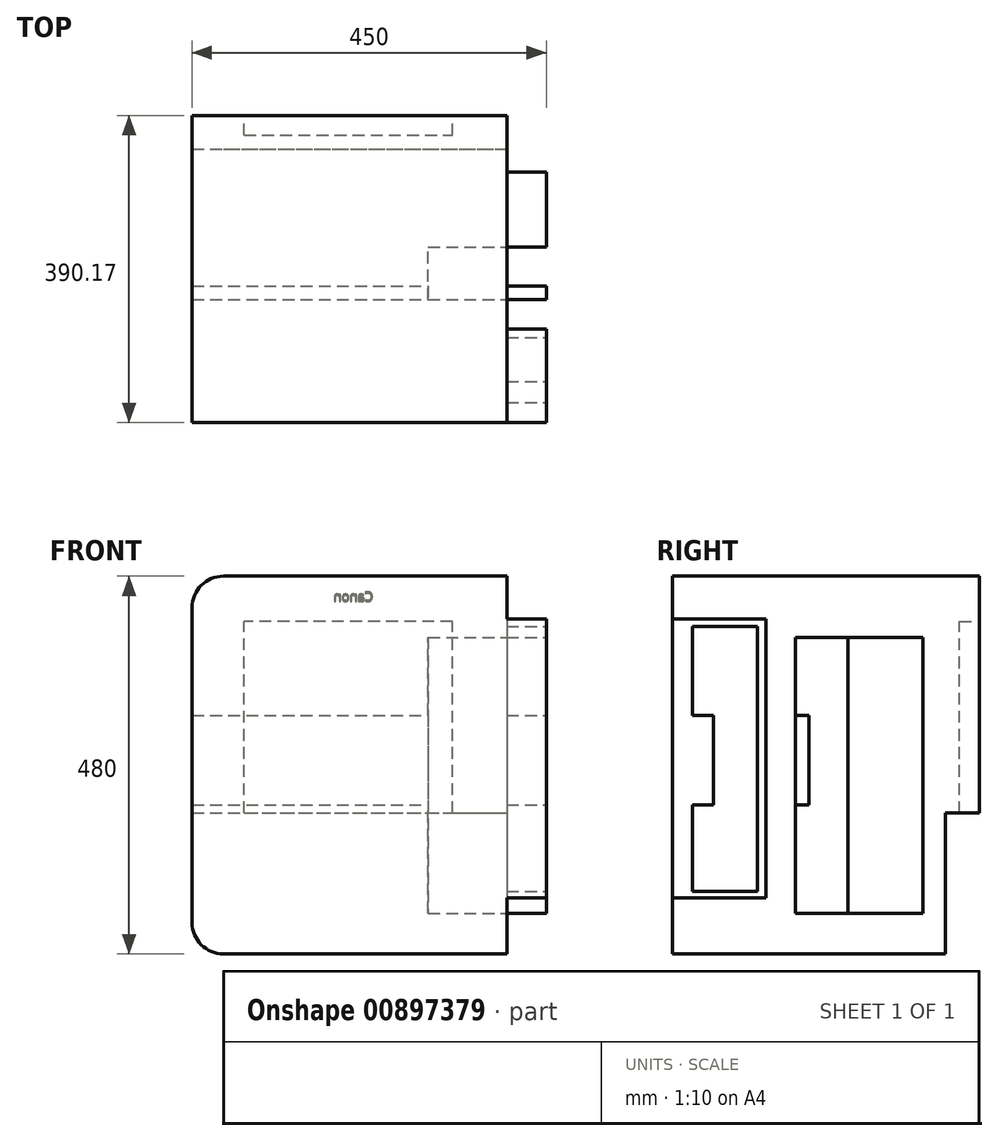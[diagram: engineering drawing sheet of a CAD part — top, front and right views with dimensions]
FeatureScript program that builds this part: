
annotation { "Feature Type Name" : "Feature", "Feature Type Description" : "" }
export const myFeature = defineFeature(function(context is Context, id is Id, definition is map)
    precondition{}
    {
        {
            var Q0;
            Q0=qCreatedBy(makeId("Top.planeOp"),FACE);
            var sketch = newSketch(context, id + "F0", { "sketchPlane" : qUnion([Q0])});
            skLineSegment(sketch, "E0.bottom", {"start": v(0, 0) * mm, "end": v(-450, 0) * mm});
            skLineSegment(sketch, "E0.top", {"start": v(0, 390) * mm, "end": v(-450, 390) * mm});
            skLineSegment(sketch, "E0.left", {"start": v(0, 0) * mm, "end": v(0, 390) * mm});
            skLineSegment(sketch, "E0.right", {"start": v(-450, 0) * mm, "end": v(-450, 390) * mm});
            skSolve(sketch);
        }
        {
            var Q0;
            Q0 = qSketchRegion(id + "F0", true);
            extrude(context, id + "F1", {"entities" : qUnion([Q0]), "depth" : 480 * mm, "offsetDistance" : 25 * mm});
        }
        {
            var Q0;
            Q0=makeQuery(id+"F1.opExtrude","SWEPT_FACE",FACE,{"disambiguationData":[OSD([sQuery(id+"F0.wireOp",EDGE,"E0.left")])]});
            var sketch = newSketch(context, id + "F2", { "sketchPlane" : qUnion([Q0])});
            skLineSegment(sketch, "E1.bottom", {"start": v(390, 480) * mm, "end": v(318.17, 480) * mm});
            skLineSegment(sketch, "E1.top", {"start": v(390, 0) * mm, "end": v(318.17, 0) * mm});
            skLineSegment(sketch, "E1.left", {"start": v(390, 480) * mm, "end": v(390, 0) * mm});
            skLineSegment(sketch, "E1.right", {"start": v(318.17, 480) * mm, "end": v(318.17, 0) * mm});
            skLineSegment(sketch, "E2.bottom", {"start": v(223.33, 480) * mm, "end": v(173.64, 480) * mm});
            skLineSegment(sketch, "E2.top", {"start": v(223.33, 0) * mm, "end": v(173.64, 0) * mm});
            skLineSegment(sketch, "E2.left", {"start": v(223.33, 480) * mm, "end": v(223.33, 0) * mm});
            skLineSegment(sketch, "E2.right", {"start": v(173.64, 480) * mm, "end": v(173.64, 0) * mm});
            skLineSegment(sketch, "E3.bottom", {"start": v(318.17, 480) * mm, "end": v(223.33, 480) * mm});
            skLineSegment(sketch, "E3.top", {"start": v(318.17, 402.26) * mm, "end": v(223.33, 402.26) * mm});
            skLineSegment(sketch, "E3.left", {"start": v(318.17, 480) * mm, "end": v(318.17, 402.26) * mm});
            skLineSegment(sketch, "E3.right", {"start": v(223.33, 480) * mm, "end": v(223.33, 402.26) * mm});
            skLineSegment(sketch, "E4.bottom", {"start": v(318.17, 0) * mm, "end": v(223.33, 0) * mm});
            skLineSegment(sketch, "E4.top", {"start": v(318.17, 51.83) * mm, "end": v(223.33, 51.83) * mm});
            skLineSegment(sketch, "E4.left", {"start": v(318.17, 0) * mm, "end": v(318.17, 51.83) * mm});
            skLineSegment(sketch, "E4.right", {"start": v(223.33, 0) * mm, "end": v(223.33, 51.83) * mm});
            skLineSegment(sketch, "E5.bottom", {"start": v(173.64, 303.3) * mm, "end": v(156.24, 303.3) * mm});
            skLineSegment(sketch, "E5.top", {"start": v(173.64, 189.66) * mm, "end": v(156.24, 189.66) * mm});
            skLineSegment(sketch, "E5.left", {"start": v(173.64, 303.3) * mm, "end": v(173.64, 189.66) * mm});
            skLineSegment(sketch, "E5.right", {"start": v(156.24, 303.3) * mm, "end": v(156.24, 189.66) * mm});
            skLineSegment(sketch, "E6.bottom", {"start": v(0, 425.5) * mm, "end": v(25.82, 425.5) * mm});
            skLineSegment(sketch, "E6.top", {"start": v(0, 71.14) * mm, "end": v(25.82, 71.14) * mm});
            skLineSegment(sketch, "E6.left", {"start": v(0, 425.5) * mm, "end": v(0, 71.14) * mm});
            skLineSegment(sketch, "E6.right", {"start": v(25.82, 425.5) * mm, "end": v(25.82, 71.14) * mm});
            skLineSegment(sketch, "E7.bottom", {"start": v(25.82, 425.5) * mm, "end": v(119.02, 425.5) * mm});
            skLineSegment(sketch, "E7.top", {"start": v(25.82, 71.14) * mm, "end": v(119.02, 71.14) * mm});
            skLineSegment(sketch, "E7.right", {"start": v(119.02, 425.5) * mm, "end": v(119.02, 71.14) * mm});
            skLineSegment(sketch, "E8.bottom", {"start": v(25.82, 416.3) * mm, "end": v(108.06, 416.3) * mm});
            skLineSegment(sketch, "E8.top", {"start": v(25.82, 79.57) * mm, "end": v(108.06, 79.57) * mm});
            skLineSegment(sketch, "E8.left", {"start": v(25.82, 416.3) * mm, "end": v(25.82, 79.57) * mm});
            skLineSegment(sketch, "E8.right", {"start": v(108.06, 416.3) * mm, "end": v(108.06, 79.57) * mm});
            skLineSegment(sketch, "E9.bottom", {"start": v(25.82, 303.3) * mm, "end": v(52.47, 303.3) * mm});
            skLineSegment(sketch, "E9.top", {"start": v(25.82, 189.66) * mm, "end": v(52.47, 189.66) * mm});
            skLineSegment(sketch, "E9.left", {"start": v(25.82, 303.3) * mm, "end": v(25.82, 189.66) * mm});
            skLineSegment(sketch, "E9.right", {"start": v(52.47, 303.3) * mm, "end": v(52.47, 189.66) * mm});
            skSolve(sketch);
        }
        {
            var Q0;
            {var subQ1=sQuery(id+"F2.wireOp",EDGE,"E2.bottom");Q0=makeQuery(id+"F2.imprint","IMPRINT",FACE,{"disambiguationData":[TD([[makeQuery(id+"F2.imprint","IMPRINT",EDGE,{"derivedFrom":subQ1}),-1.0]])]});}
            var Q1;
            {var subQ2=sQuery(id+"F2.wireOp",EDGE,"E5.bottom");Q1=makeQuery(id+"F2.imprint","IMPRINT",FACE,{"disambiguationData":[TD([[makeQuery(id+"F2.imprint","IMPRINT",EDGE,{"derivedFrom":subQ2}),-1.0]])]});}
            var Q2;
            {var subQ5=sQuery(id+"F2.wireOp",EDGE,"E8.bottom");Q2=makeQuery(id+"F2.imprint","IMPRINT",FACE,{"disambiguationData":[TD([[makeQuery(id+"F2.imprint","IMPRINT",EDGE,{"derivedFrom":subQ5}),-1.0]])]});}
            var Q3;
            Q3=makeQuery(id+"F2.imprint","IMPRINT",FACE,{"disambiguationData":[TD([[makeQuery(id+"F2.imprint","IMPRINT",EDGE,{"derivedFrom":sQuery(id+"F2.wireOp",EDGE,"E1.bottom")}),-1.0]])]});
            var Q4;
            Q4=makeQuery(id+"F2.imprint","IMPRINT",FACE,{"disambiguationData":[TD([[makeQuery(id+"F2.imprint","IMPRINT",EDGE,{"derivedFrom":sQuery(id+"F2.wireOp",EDGE,"E4.bottom")}),1.0]])]});
            var Q5;
            Q5=makeQuery(id+"F2.imprint","IMPRINT",FACE,{"disambiguationData":[TD([[makeQuery(id+"F2.imprint","IMPRINT",EDGE,{"derivedFrom":sQuery(id+"F2.wireOp",EDGE,"E3.bottom")}),-1.0]])]});
            extrude(context, id + "F3", {"entities" : qUnion([Q0, Q1, Q2, Q3, Q4, Q5]), "operationType" : NewBodyOperationType.REMOVE, "oppositeDirection" : true, "depth" : 50 * mm, "offsetDistance" : 25 * mm});
        }
        {
            var Q0;
            Q0=makeQuery(id+"F3.boolean.opBoolean","COPY",FACE,{"derivedFrom":makeQuery(id+"F3.opExtrude","CAP_FACE",FACE,{"disambiguationData":[OSD([sQuery(id+"F0.wireOp",EDGE,"E0.bottom"),sQuery(id+"F0.wireOp",EDGE,"E0.left"),sQuery(id+"F2.wireOp",EDGE,"E1.bottom"),sQuery(id+"F2.wireOp",EDGE,"E1.top"),sQuery(id+"F2.wireOp",EDGE,"E1.left"),sQuery(id+"F2.wireOp",EDGE,"E1.right"),sQuery(id+"F2.wireOp",EDGE,"E2.bottom"),sQuery(id+"F2.wireOp",EDGE,"E2.top"),sQuery(id+"F2.wireOp",EDGE,"E2.left"),sQuery(id+"F2.wireOp",EDGE,"E3.bottom"),sQuery(id+"F2.wireOp",EDGE,"E3.top"),sQuery(id+"F2.wireOp",EDGE,"E4.bottom"),sQuery(id+"F2.wireOp",EDGE,"E4.top"),sQuery(id+"F2.wireOp",EDGE,"E5.bottom"),sQuery(id+"F2.wireOp",EDGE,"E5.top"),sQuery(id+"F2.wireOp",EDGE,"E5.left"),sQuery(id+"F2.wireOp",EDGE,"E5.right"),sQuery(id+"F2.wireOp",EDGE,"E6.bottom"),sQuery(id+"F2.wireOp",EDGE,"E6.top"),sQuery(id+"F2.wireOp",EDGE,"E7.bottom"),sQuery(id+"F2.wireOp",EDGE,"E7.top"),sQuery(id+"F2.wireOp",EDGE,"E7.right")])],"isStart":false})});
            var sketch = newSketch(context, id + "F4", { "sketchPlane" : qUnion([Q0])});
            skLineSegment(sketch, "E10.bottom", {"start": v(156.24, 51.83) * mm, "end": v(223.33, 51.83) * mm});
            skLineSegment(sketch, "E10.top", {"start": v(156.24, 402.26) * mm, "end": v(223.33, 402.26) * mm});
            skLineSegment(sketch, "E10.left", {"start": v(156.24, 51.83) * mm, "end": v(156.24, 402.26) * mm});
            skLineSegment(sketch, "E10.right", {"start": v(223.33, 51.83) * mm, "end": v(223.33, 402.26) * mm});
            skLineSegment(sketch, "E11.bottom", {"start": v(390, 178.91) * mm, "end": v(347.26, 178.91) * mm});
            skLineSegment(sketch, "E11.top", {"start": v(390, 0) * mm, "end": v(347.26, 0) * mm});
            skLineSegment(sketch, "E11.left", {"start": v(390, 178.91) * mm, "end": v(390, 0) * mm});
            skLineSegment(sketch, "E11.right", {"start": v(347.26, 178.91) * mm, "end": v(347.26, 0) * mm});
            skSolve(sketch);
        }
        {
            var Q0;
            Q0=makeQuery(id+"F4.imprint","IMPRINT",FACE,{"disambiguationData":[TD([[makeQuery(id+"F4.imprint","IMPRINT",EDGE,{"derivedFrom":sQuery(id+"F4.wireOp",EDGE,"E11.bottom")}),1.0]])]});
            var Q1;
            {var subQ1=makeQuery(id+"F3.boolean.opBoolean","COPY",EDGE,{"derivedFrom":makeQuery(id+"F3.opExtrude","CAP_EDGE",EDGE,{"disambiguationData":[OSD([sQuery(id+"F2.wireOp",EDGE,"E5.bottom")])],"isStart":false})});Q1=makeQuery(id+"F4.imprint","IMPRINT",FACE,{"disambiguationData":[TD([[makeQuery(id+"F4.imprint","IMPRINT",EDGE,{"derivedFrom":subQ1}),1.0]])]});}
            extrude(context, id + "F5", {"entities" : qUnion([Q0, Q1]), "operationType" : NewBodyOperationType.REMOVE, "oppositeDirection" : true, "depth" : 400 * mm, "offsetDistance" : 25 * mm});
        }
        {
            var Q0;
            {var subQ4=sQuery(id+"F4.wireOp",EDGE,"E10.bottom");Q0=makeQuery(id+"F4.imprint","IMPRINT",FACE,{"disambiguationData":[TD([[makeQuery(id+"F4.imprint","IMPRINT",EDGE,{"derivedFrom":subQ4}),1.0]])]});}
            extrude(context, id + "F6", {"entities" : qUnion([Q0]), "operationType" : NewBodyOperationType.REMOVE, "oppositeDirection" : true, "depth" : 100 * mm, "offsetDistance" : 25 * mm});
        }
        {
            var Q0;
            Q0=makeQuery(id+"F1.opExtrude","SWEPT_FACE",FACE,{"disambiguationData":[OSD([sQuery(id+"F0.wireOp",EDGE,"E0.top")])]});
            var sketch = newSketch(context, id + "F7", { "sketchPlane" : qUnion([Q0])});
            skLineSegment(sketch, "E12.bottom", {"start": v(119.36, 178.91) * mm, "end": v(383.88, 178.91) * mm});
            skLineSegment(sketch, "E12.top", {"start": v(119.36, 422.37) * mm, "end": v(383.88, 422.37) * mm});
            skLineSegment(sketch, "E12.left", {"start": v(119.36, 178.91) * mm, "end": v(119.36, 422.37) * mm});
            skLineSegment(sketch, "E12.right", {"start": v(383.88, 178.91) * mm, "end": v(383.88, 422.37) * mm});
            skSolve(sketch);
        }
        {
            var Q0;
            Q0 = qSketchRegion(id + "F7", true);
            extrude(context, id + "F8", {"entities" : qUnion([Q0]), "operationType" : NewBodyOperationType.REMOVE, "oppositeDirection" : true, "depth" : 25 * mm, "offsetDistance" : 25 * mm});
        }
        {
            var Q0;
            Q0=makeQuery(id+"F3.boolean.opBoolean","COPY",EDGE,{"derivedFrom":makeQuery(id+"F3.opExtrude","CAP_EDGE",EDGE,{"disambiguationData":[OSD([sQuery(id+"F0.wireOp",EDGE,"E0.left"),sQuery(id+"F2.wireOp",EDGE,"E1.bottom"),sQuery(id+"F2.wireOp",EDGE,"E2.bottom"),sQuery(id+"F2.wireOp",EDGE,"E3.bottom")])],"isStart":false})});
            var Q1;
            Q1=makeQuery(id+"F5.boolean.opBoolean","COPY",EDGE,{"derivedFrom":makeQuery(id+"F5.opExtrude","CAP_EDGE",EDGE,{"disambiguationData":[OSD([sQuery(id+"F4.wireOp",EDGE,"E11.bottom")])],"isStart":true})});
            var Q2;
            Q2=makeQuery(id+"F3.boolean.opBoolean","COPY",EDGE,{"derivedFrom":makeQuery(id+"F3.opExtrude","CAP_EDGE",EDGE,{"disambiguationData":[OSD([sQuery(id+"F0.wireOp",EDGE,"E0.left"),sQuery(id+"F2.wireOp",EDGE,"E1.top"),sQuery(id+"F2.wireOp",EDGE,"E2.top"),sQuery(id+"F2.wireOp",EDGE,"E4.bottom")])],"isStart":false})});
            var Q3;
            Q3=makeQuery(id+"F1.opExtrude","CAP_EDGE",EDGE,{"disambiguationData":[OSD([sQuery(id+"F0.wireOp",EDGE,"E0.right")])],"isStart":true});
            var Q4;
            Q4=makeQuery(id+"F5.boolean.opBoolean","COPY",EDGE,{"derivedFrom":makeQuery(id+"F5.opExtrude","CAP_EDGE",EDGE,{"disambiguationData":[OSD([sQuery(id+"F4.wireOp",EDGE,"E11.bottom")])],"isStart":false})});
            var Q5;
            Q5=makeQuery(id+"F1.opExtrude","CAP_EDGE",EDGE,{"disambiguationData":[OSD([sQuery(id+"F0.wireOp",EDGE,"E0.right")])],"isStart":false});
            fillet(context, id + "F9", {"entities" : qUnion([Q0, Q1, Q2, Q3, Q4, Q5]), "radius" : 40 * mm, "tangentPropagation" : true, "allowEdgeOverflow" : false});
        }
        {
            var Q0;
            Q0=makeQuery(id+"F3.boolean.opBoolean","COPY",FACE,{"derivedFrom":makeQuery(id+"F3.opExtrude","SWEPT_FACE",FACE,{"disambiguationData":[OSD([sQuery(id+"F2.wireOp",EDGE,"E1.right")])]})});
            var sketch = newSketch(context, id + "F10", { "sketchPlane" : qUnion([Q0])});
            skText(sketch, "E13", { "text": "Canon\n", "fontName": "OpenSans-Regular.ttf"});
            const initialGuessF10  = {"E13": [0.22, 0.44801, 1, 0, 0.01199]};
            skSetInitialGuess(sketch, initialGuessF10);
            skSolve(sketch);
        }
        {
            var Q0;
            Q0 = qSketchRegion(id + "F10", true);
            extrude(context, id + "F11", {"entities" : qUnion([Q0]), "operationType" : NewBodyOperationType.ADD, "depth" : 72 * mm, "offsetDistance" : 25 * mm});
        }
    });
